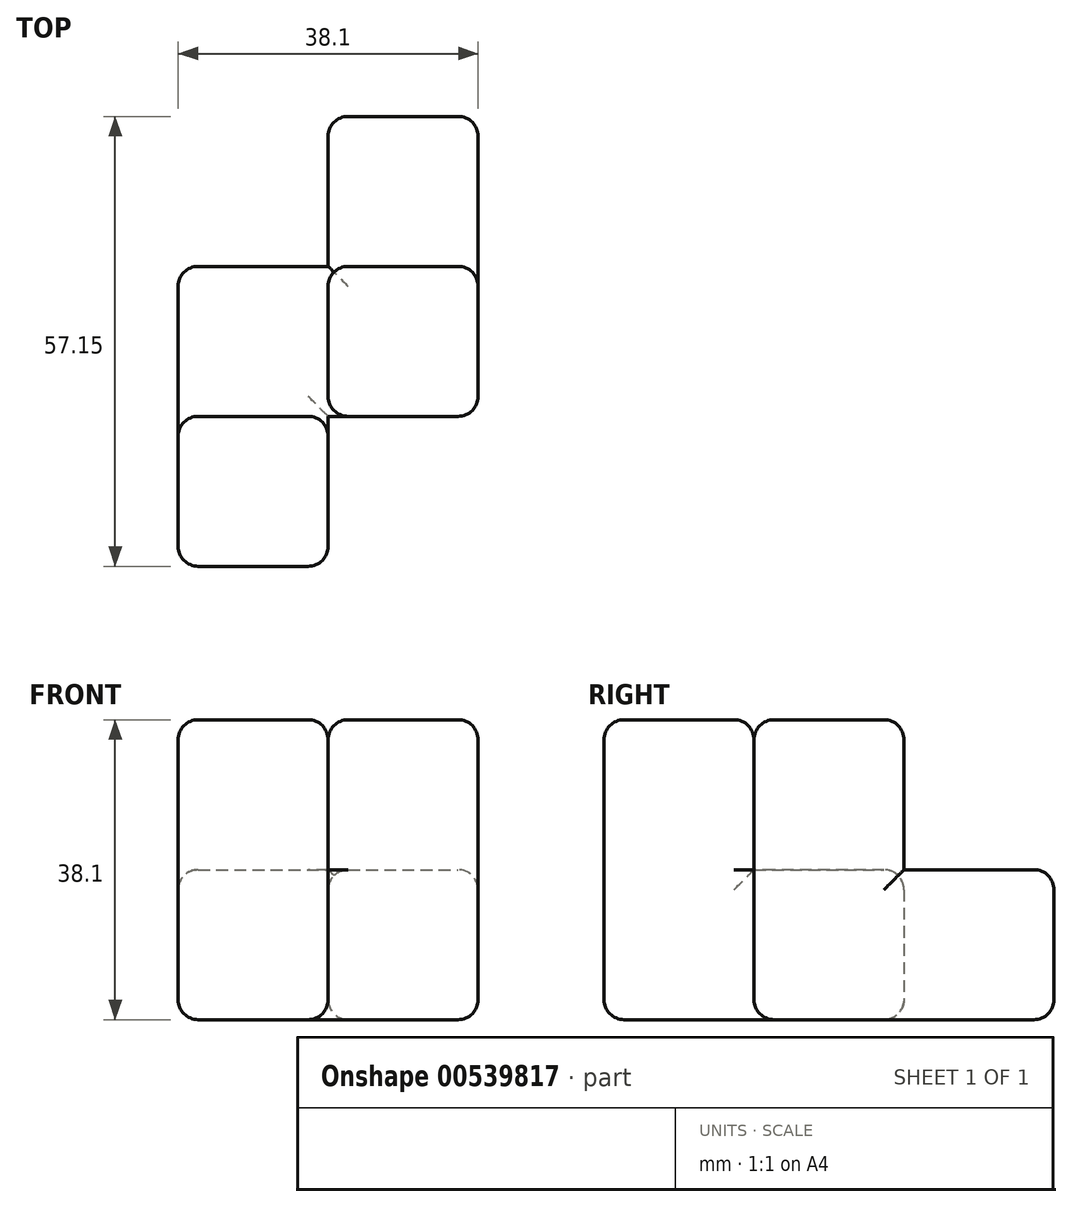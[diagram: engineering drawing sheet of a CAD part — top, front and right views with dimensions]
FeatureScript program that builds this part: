
annotation { "Feature Type Name" : "Feature", "Feature Type Description" : "" }
export const myFeature = defineFeature(function(context is Context, id is Id, definition is map)
    precondition{}
    {
        {
            var Q0;
            Q0=qCreatedBy(makeId("Top.planeOp"),FACE);
            var sketch = newSketch(context, id + "F0", { "sketchPlane" : qUnion([Q0])});
            skLineSegment(sketch, "E0", {"start": v(0, 0) * mm, "end": v(0, 38.1) * mm});
            skLineSegment(sketch, "E1", {"start": v(0, 38.1) * mm, "end": v(19.05, 38.1) * mm});
            skLineSegment(sketch, "E2", {"start": v(19.05, 38.1) * mm, "end": v(19.05, 57.15) * mm});
            skLineSegment(sketch, "E3", {"start": v(19.05, 57.15) * mm, "end": v(38.1, 57.15) * mm});
            skLineSegment(sketch, "E4", {"start": v(38.1, 57.15) * mm, "end": v(38.1, 19.05) * mm});
            skLineSegment(sketch, "E5", {"start": v(38.1, 19.05) * mm, "end": v(19.05, 19.05) * mm});
            skLineSegment(sketch, "E6", {"start": v(19.05, 19.05) * mm, "end": v(19.05, 0) * mm});
            skLineSegment(sketch, "E7", {"start": v(19.05, 0) * mm, "end": v(0, 0) * mm});
            skSolve(sketch);
        }
        {
            var Q0;
            Q0=makeQuery(id+"F0.imprint","IMPRINT",FACE,{"disambiguationData":[TD([[makeQuery(id+"F0.imprint","IMPRINT",EDGE,{"derivedFrom":sQuery(id+"F0.wireOp",EDGE,"E0")}),-1.0]])]});
            extrude(context, id + "F1", {"entities" : qUnion([Q0]), "depth" : 19.05 * mm, "offsetDistance" : 25.4 * mm});
        }
        {
            var Q0;
            Q0=makeQuery(id+"F1.opExtrude","CAP_FACE",FACE,{"disambiguationData":[OSD([sQuery(id+"F0.wireOp",EDGE,"E0"),sQuery(id+"F0.wireOp",EDGE,"E1"),sQuery(id+"F0.wireOp",EDGE,"E2"),sQuery(id+"F0.wireOp",EDGE,"E3"),sQuery(id+"F0.wireOp",EDGE,"E4"),sQuery(id+"F0.wireOp",EDGE,"E5"),sQuery(id+"F0.wireOp",EDGE,"E6"),sQuery(id+"F0.wireOp",EDGE,"E7")])],"isStart":false});
            var sketch = newSketch(context, id + "F2", { "sketchPlane" : qUnion([Q0])});
            skLineSegment(sketch, "E8.bottom", {"start": v(0, 0) * mm, "end": v(19.05, 0) * mm});
            skLineSegment(sketch, "E8.top", {"start": v(0, 19.05) * mm, "end": v(19.05, 19.05) * mm});
            skLineSegment(sketch, "E8.left", {"start": v(0, 0) * mm, "end": v(0, 19.05) * mm});
            skLineSegment(sketch, "E8.right", {"start": v(19.05, 0) * mm, "end": v(19.05, 19.05) * mm});
            skLineSegment(sketch, "E9.bottom", {"start": v(19.05, 38.1) * mm, "end": v(38.1, 38.1) * mm});
            skLineSegment(sketch, "E9.top", {"start": v(19.05, 19.05) * mm, "end": v(38.1, 19.05) * mm});
            skLineSegment(sketch, "E9.left", {"start": v(19.05, 38.1) * mm, "end": v(19.05, 19.05) * mm});
            skLineSegment(sketch, "E9.right", {"start": v(38.1, 38.1) * mm, "end": v(38.1, 19.05) * mm});
            skSolve(sketch);
        }
        {
            var Q0;
            Q0=makeQuery(id+"F2.imprint","IMPRINT",FACE,{"disambiguationData":[TD([[makeQuery(id+"F2.imprint","IMPRINT",EDGE,{"derivedFrom":sQuery(id+"F2.wireOp",EDGE,"E8.bottom")}),-1.0]])]});
            extrude(context, id + "F3", {"entities" : qUnion([Q0]), "operationType" : NewBodyOperationType.ADD, "depth" : 19.05 * mm, "offsetDistance" : 25.4 * mm});
        }
        {
            var Q0;
            Q0=makeQuery(id+"F3.opExtrude","SWEPT_EDGE",EDGE,{"disambiguationData":[OSD([sQuery(id+"F2.wireOp",EDGE,"E8.top"),sQuery(id+"F2.wireOp",EDGE,"E8.right"),sQuery(id+"F2.wireOp",EDGE,"E9.top"),sQuery(id+"F2.wireOp",EDGE,"E9.left")])]});
            fillet(context, id + "F4", {"entities" : qUnion([Q0]), "radius" : 2.54 * mm, "tangentPropagation" : true, "allowEdgeOverflow" : false});
        }
        {
            var Q0;
            Q0=makeQuery(id+"F2.imprint","IMPRINT",FACE,{"disambiguationData":[TD([[makeQuery(id+"F2.imprint","IMPRINT",EDGE,{"derivedFrom":sQuery(id+"F2.wireOp",EDGE,"E9.bottom")}),-1.0]])]});
            extrude(context, id + "F5", {"entities" : qUnion([Q0]), "operationType" : NewBodyOperationType.ADD, "depth" : 19.05 * mm, "offsetDistance" : 25.4 * mm});
        }
        {
            var Q0;
            Q0=makeQuery(id+"F1.opExtrude","CAP_FACE",FACE,{"disambiguationData":[OSD([sQuery(id+"F0.wireOp",EDGE,"E0"),sQuery(id+"F0.wireOp",EDGE,"E1"),sQuery(id+"F0.wireOp",EDGE,"E2"),sQuery(id+"F0.wireOp",EDGE,"E3"),sQuery(id+"F0.wireOp",EDGE,"E4"),sQuery(id+"F0.wireOp",EDGE,"E5"),sQuery(id+"F0.wireOp",EDGE,"E6"),sQuery(id+"F0.wireOp",EDGE,"E7")])],"isStart":true});
            var Q1;
            Q1=makeQuery(id+"F3.boolean.opBoolean","MERGE",FACE,{"derivedFrom":[makeQuery(id+"F1.opExtrude","SWEPT_FACE",FACE,{"disambiguationData":[OSD([sQuery(id+"F0.wireOp",EDGE,"E7")])]}),makeQuery(id+"F3.opExtrude","SWEPT_FACE",FACE,{"disambiguationData":[OSD([sQuery(id+"F2.wireOp",EDGE,"E8.bottom")])]})]});
            var Q2;
            Q2=makeQuery(id+"F5.boolean.opBoolean","MERGE",FACE,{"derivedFrom":[makeQuery(id+"F1.opExtrude","SWEPT_FACE",FACE,{"disambiguationData":[OSD([sQuery(id+"F0.wireOp",EDGE,"E4")])]}),makeQuery(id+"F5.opExtrude","SWEPT_FACE",FACE,{"disambiguationData":[OSD([sQuery(id+"F2.wireOp",EDGE,"E9.right")])]})]});
            var Q3;
            Q3=makeQuery(id+"F3.boolean.opBoolean","MERGE",FACE,{"derivedFrom":[makeQuery(id+"F1.opExtrude","SWEPT_FACE",FACE,{"disambiguationData":[OSD([sQuery(id+"F0.wireOp",EDGE,"E0")])]}),makeQuery(id+"F3.opExtrude","SWEPT_FACE",FACE,{"disambiguationData":[OSD([sQuery(id+"F2.wireOp",EDGE,"E8.left")])]})]});
            var Q4;
            Q4=makeQuery(id+"F3.opExtrude","CAP_FACE",FACE,{"disambiguationData":[OSD([sQuery(id+"F2.wireOp",EDGE,"E8.bottom"),sQuery(id+"F2.wireOp",EDGE,"E8.top"),sQuery(id+"F2.wireOp",EDGE,"E8.left"),sQuery(id+"F2.wireOp",EDGE,"E8.right")])],"isStart":false});
            var Q5;
            Q5=makeQuery(id+"F5.opExtrude","CAP_FACE",FACE,{"disambiguationData":[OSD([sQuery(id+"F2.wireOp",EDGE,"E9.bottom"),sQuery(id+"F2.wireOp",EDGE,"E9.top"),sQuery(id+"F2.wireOp",EDGE,"E9.left"),sQuery(id+"F2.wireOp",EDGE,"E9.right")])],"isStart":false});
            var Q6;
            Q6=makeQuery(id+"F1.opExtrude","SWEPT_FACE",FACE,{"disambiguationData":[OSD([sQuery(id+"F0.wireOp",EDGE,"E3")])]});
            var Q7;
            Q7=makeQuery(id+"F5.opExtrude","SWEPT_EDGE",EDGE,{"disambiguationData":[OSD([sQuery(id+"F2.wireOp",EDGE,"E8.top"),sQuery(id+"F2.wireOp",EDGE,"E8.right"),sQuery(id+"F2.wireOp",EDGE,"E9.top"),sQuery(id+"F2.wireOp",EDGE,"E9.left")])]});
            fillet(context, id + "F6", {"entities" : qUnion([Q0, Q1, Q2, Q3, Q4, Q5, Q6, Q7]), "radius" : 2.54 * mm, "tangentPropagation" : true, "allowEdgeOverflow" : false});
        }
        {
            var Q0;
            Q0=makeQuery(id+"F1.opExtrude","CAP_EDGE",EDGE,{"disambiguationData":[OSD([sQuery(id+"F0.wireOp",EDGE,"E2")])],"isStart":false});
            fillet(context, id + "F7", {"entities" : qUnion([Q0]), "radius" : 2.54 * mm, "tangentPropagation" : true, "allowEdgeOverflow" : false});
        }
        {
            var Q0;
            Q0=makeQuery(id+"F5.opExtrude","SWEPT_EDGE",EDGE,{"disambiguationData":[OSD([sQuery(id+"F0.wireOp",EDGE,"E1"),sQuery(id+"F0.wireOp",EDGE,"E2"),sQuery(id+"F2.wireOp",EDGE,"E9.bottom"),sQuery(id+"F2.wireOp",EDGE,"E9.left")])]});
            fillet(context, id + "F8", {"entities" : qUnion([Q0]), "radius" : 2.54 * mm, "tangentPropagation" : true, "allowEdgeOverflow" : false});
        }
        {
            var Q0;
            Q0=makeQuery(id+"F1.opExtrude","CAP_EDGE",EDGE,{"disambiguationData":[OSD([sQuery(id+"F0.wireOp",EDGE,"E1")])],"isStart":false});
            fillet(context, id + "F9", {"entities" : qUnion([Q0]), "radius" : 2.54 * mm, "tangentPropagation" : true, "allowEdgeOverflow" : false});
        }
    });
